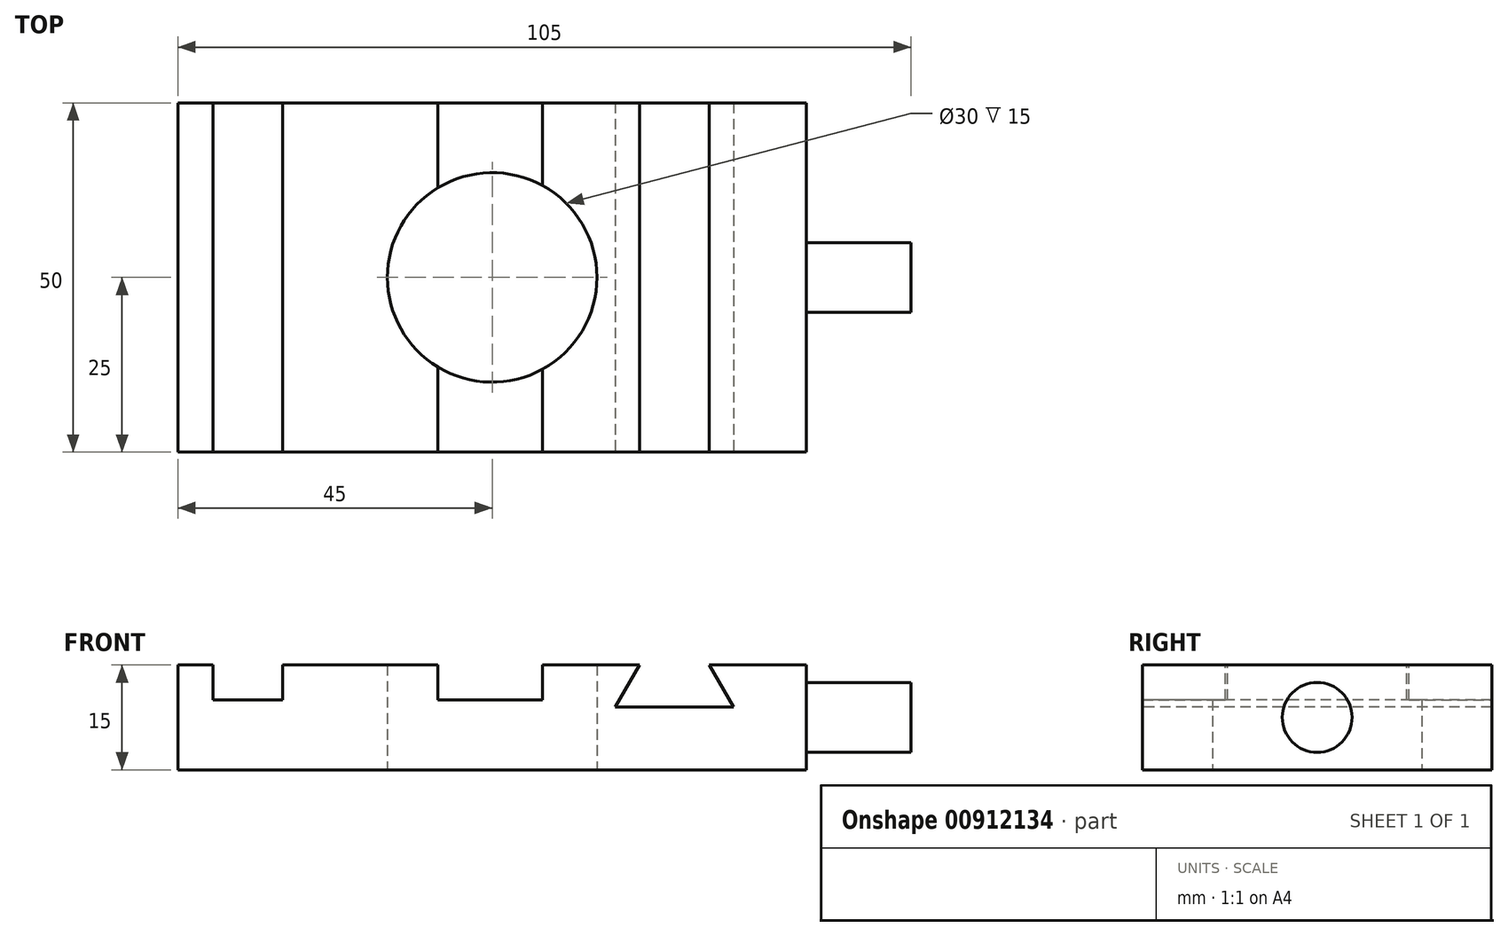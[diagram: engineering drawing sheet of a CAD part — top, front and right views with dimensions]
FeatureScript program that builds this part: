
annotation { "Feature Type Name" : "Feature", "Feature Type Description" : "" }
export const myFeature = defineFeature(function(context is Context, id is Id, definition is map)
    precondition{}
    {
        {
            var Q0;
            Q0=qCreatedBy(makeId("Top.planeOp"),FACE);
            var sketch = newSketch(context, id + "F0", { "sketchPlane" : qUnion([Q0])});
            skPoint(sketch, "E0.middle", {"position": v(0, 0) * mm});
            skLineSegment(sketch, "E1.bottom", {"start": v(45, 25) * mm, "end": v(-45, 25) * mm});
            skLineSegment(sketch, "E1.top", {"start": v(45, -25) * mm, "end": v(-45, -25) * mm});
            skLineSegment(sketch, "E1.left", {"start": v(45, 25) * mm, "end": v(45, -25) * mm});
            skLineSegment(sketch, "E1.right", {"start": v(-45, 25) * mm, "end": v(-45, -25) * mm});
            skCircle(sketch, "E2", {"center": v(0, 0) * mm, "radius": 15 * mm});
            skSolve(sketch);
        }
        {
            var Q0;
            Q0=makeQuery(id+"F0.imprint","IMPRINT",FACE,{"disambiguationData":[TD([[makeQuery(id+"F0.imprint","IMPRINT",EDGE,{"derivedFrom":sQuery(id+"F0.wireOp",EDGE,"E1.bottom")}),1.0]])]});
            extrude(context, id + "F1", {"entities" : qUnion([Q0]), "depth" : 15 * mm, "offsetDistance" : 25 * mm});
        }
        {
            var Q0;
            Q0=makeQuery(id+"F1.opExtrude","CAP_FACE",FACE,{"disambiguationData":[OSD([sQuery(id+"F0.wireOp",EDGE,"E1.bottom"),sQuery(id+"F0.wireOp",EDGE,"E1.top"),sQuery(id+"F0.wireOp",EDGE,"E1.left"),sQuery(id+"F0.wireOp",EDGE,"E1.right"),sQuery(id+"F0.wireOp",EDGE,"E2")])],"isStart":false});
            var sketch = newSketch(context, id + "F2", { "sketchPlane" : qUnion([Q0])});
            skLineSegment(sketch, "E3.bottom", {"start": v(-40, 25) * mm, "end": v(-30, 25) * mm});
            skLineSegment(sketch, "E3.top", {"start": v(-40, -25) * mm, "end": v(-30, -25) * mm});
            skLineSegment(sketch, "E3.left", {"start": v(-40, 25) * mm, "end": v(-40, -25) * mm});
            skLineSegment(sketch, "E3.right", {"start": v(-30, 25) * mm, "end": v(-30, -25) * mm});
            skLineSegment(sketch, "E4", {"start": v(-7.79, 25) * mm, "end": v(-7.79, -25) * mm});
            skLineSegment(sketch, "E5", {"start": v(-7.79, -25) * mm, "end": v(7.21, -25) * mm});
            skLineSegment(sketch, "E6", {"start": v(7.21, -25) * mm, "end": v(7.21, 25) * mm});
            skLineSegment(sketch, "E7", {"start": v(7.21, 25) * mm, "end": v(-7.79, 25) * mm});
            skPoint(sketch, "E8", {"position": v(0, 0) * mm});
            skSolve(sketch);
        }
        {
            var Q0;
            Q0=makeQuery(id+"F2.imprint","IMPRINT",FACE,{"disambiguationData":[TD([[makeQuery(id+"F2.imprint","IMPRINT",EDGE,{"derivedFrom":sQuery(id+"F2.wireOp",EDGE,"E3.bottom")}),1.0]])]});
            var Q1;
            {var subQ0=sQuery(id+"F2.wireOp",EDGE,"E5");Q1=makeQuery(id+"F2.imprint","IMPRINT",FACE,{"disambiguationData":[TD([[makeQuery(id+"F2.imprint","IMPRINT",EDGE,{"derivedFrom":subQ0}),-1.0]])]});}
            var Q2;
            {var subQ0=sQuery(id+"F2.wireOp",EDGE,"E7");Q2=makeQuery(id+"F2.imprint","IMPRINT",FACE,{"disambiguationData":[TD([[makeQuery(id+"F2.imprint","IMPRINT",EDGE,{"derivedFrom":subQ0}),1.0]])]});}
            extrude(context, id + "F3", {"entities" : qUnion([Q0, Q1, Q2]), "operationType" : NewBodyOperationType.REMOVE, "oppositeDirection" : true, "depth" : 5 * mm, "offsetDistance" : 25 * mm});
        }
        {
            var Q0;
            Q0=makeQuery(id+"F1.opExtrude","SWEPT_FACE",FACE,{"disambiguationData":[OSD([sQuery(id+"F0.wireOp",EDGE,"E1.top")])]});
            var sketch = newSketch(context, id + "F4", { "sketchPlane" : qUnion([Q0])});
            skSolve(sketch);
        }
        {
            var Q0;
            {var subQ3=sQuery(id+"F0.wireOp",EDGE,"E1.top");Q0=makeQuery(id+"F4.imprint","IMPRINT",FACE,{"disambiguationData":[TD([[makeQuery(id+"F4.imprint","IMPRINT",EDGE,{"derivedFrom":makeQuery(id+"F1.opExtrude","CAP_EDGE",EDGE,{"disambiguationData":[OSD([subQ3])],"isStart":true})}),-1.0]])]});}
            var sketch = newSketch(context, id + "F5", { "sketchPlane" : qUnion([Q0])});
            skLineSegment(sketch, "E9", {"start": v(21.1, 15) * mm, "end": v(17.64, 9) * mm});
            skLineSegment(sketch, "E10", {"start": v(17.64, 9) * mm, "end": v(34.57, 9) * mm});
            skLineSegment(sketch, "E11", {"start": v(34.57, 9) * mm, "end": v(31.1, 15) * mm});
            skLineSegment(sketch, "E12", {"start": v(31.1, 15) * mm, "end": v(21.1, 15) * mm});
            skLineSegment(sketch, "E13", {"start": v(26.1, 9) * mm, "end": v(26.1, 15) * mm, "construction": true});
            skSolve(sketch);
        }
        {
            var Q0;
            Q0=makeQuery(id+"F5.imprint","IMPRINT",FACE,{"disambiguationData":[TD([[makeQuery(id+"F5.imprint","IMPRINT",EDGE,{"derivedFrom":sQuery(id+"F5.wireOp",EDGE,"E9")}),1.0]])]});
            extrude(context, id + "F6", {"entities" : qUnion([Q0]), "operationType" : NewBodyOperationType.REMOVE, "oppositeDirection" : true, "depth" : 50 * mm, "offsetDistance" : 25 * mm});
        }
        {
            var Q0;
            Q0=makeQuery(id+"F1.opExtrude","SWEPT_FACE",FACE,{"disambiguationData":[OSD([sQuery(id+"F0.wireOp",EDGE,"E1.left")])]});
            var sketch = newSketch(context, id + "F7", { "sketchPlane" : qUnion([Q0])});
            skCircle(sketch, "E14", {"center": v(0, 7.5) * mm, "radius": 5 * mm});
            skPoint(sketch, "E14.centerSnap0", {"position": v(-25, 7.5) * mm});
            skPoint(sketch, "E14.centerSnap1", {"position": v(0, 15) * mm});
            skSolve(sketch);
        }
        {
            var Q0;
            Q0=makeQuery(id+"F7.imprint","IMPRINT",FACE,{"disambiguationData":[TD([[makeQuery(id+"F7.imprint","IMPRINT",EDGE,{"derivedFrom":sQuery(id+"F7.wireOp",EDGE,"E14")}),1.0]])]});
            extrude(context, id + "F8", {"entities" : qUnion([Q0]), "operationType" : NewBodyOperationType.ADD, "depth" : 15 * mm, "offsetDistance" : 25 * mm});
        }
    });
